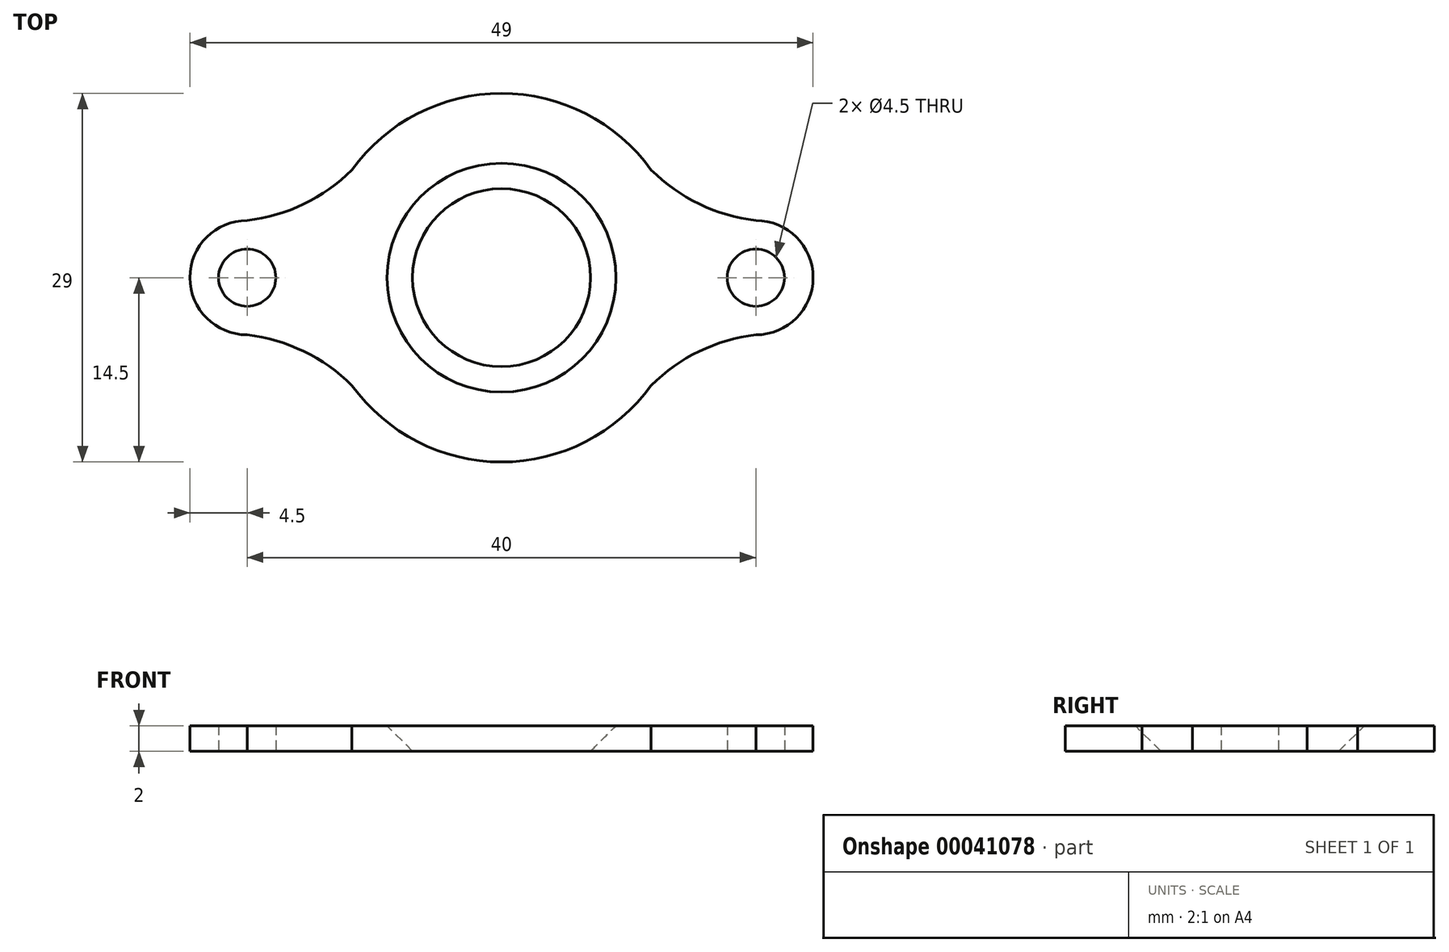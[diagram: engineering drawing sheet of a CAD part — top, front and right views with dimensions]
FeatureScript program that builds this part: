
annotation { "Feature Type Name" : "Feature", "Feature Type Description" : "" }
export const myFeature = defineFeature(function(context is Context, id is Id, definition is map)
    precondition{}
    {
        {
            var Q0;
            Q0=qCreatedBy(makeId("Top.planeOp"),FACE);
            var sketch = newSketch(context, id + "F0", { "sketchPlane" : qUnion([Q0])});
            skLineSegment(sketch, "E0", {"start": v(-20, 0) * mm, "end": v(20, 0) * mm, "construction": true});
            skCircle(sketch, "E1", {"center": v(0, 0) * mm, "radius": 7 * mm});
            skCircle(sketch, "E2", {"center": v(0, 0) * mm, "radius": 14.5 * mm});
            skCircle(sketch, "E3", {"center": v(-20, 0) * mm, "radius": 2.25 * mm});
            skCircle(sketch, "E4", {"center": v(20, 0) * mm, "radius": 2.25 * mm});
            skLineSegment(sketch, "E5", {"start": v(-20, 4.5) * mm, "end": v(-20, -4.5) * mm, "construction": true});
            skLineSegment(sketch, "E6", {"start": v(0, 4.5) * mm, "end": v(0, -4.5) * mm, "construction": true});
            skLineSegment(sketch, "E7.MirrorCS", {"start": v(20, 4.5) * mm, "end": v(20, -4.5) * mm, "construction": true});
            skArc(sketch, "E8", {"start": v(-20, 4.5) * mm, "mid": v(-24.5, 0) * mm, "end": v(-20, -4.5) * mm});
            skLineSegment(sketch, "E9", {"start": v(0, 0) * mm, "end": v(-10.25, 10.25) * mm, "construction": true});
            skArc(sketch, "E10", {"start": v(-20, 4.5) * mm, "mid": v(-14.52, 6.35) * mm, "end": v(-10.25, 10.25) * mm});
            skArc(sketch, "E11.MirrorCS", {"start": v(-20, -4.5) * mm, "mid": v(-14.52, -6.35) * mm, "end": v(-10.25, -10.25) * mm});
            skArc(sketch, "E12.MirrorCS", {"start": v(20, 4.5) * mm, "mid": v(14.52, 6.35) * mm, "end": v(10.25, 10.25) * mm});
            skArc(sketch, "E13.MirrorCS", {"start": v(20, 4.5) * mm, "mid": v(24.5, 0) * mm, "end": v(20, -4.5) * mm});
            skArc(sketch, "E14.MirrorCS", {"start": v(20, -4.5) * mm, "mid": v(14.52, -6.35) * mm, "end": v(10.25, -10.25) * mm});
            skSolve(sketch);
        }
        {
            var Q0;
            Q0 = qSketchRegion(id + "F0", true);
            extrude(context, id + "F1", {"entities" : qUnion([Q0]), "depth" : 2 * mm});
        }
        {
            var Q0;
            Q0=makeQuery(id+"F1.opExtrude","CAP_EDGE",EDGE,{"disambiguationData":[OSD([sQuery(id+"F0.wireOp",EDGE,"E1")])],"isStart":false});
            chamfer(context, id + "F2", {"entities" : qUnion([Q0]), "width" : 2 * mm, "tangentPropagation" : true});
        }
    });
